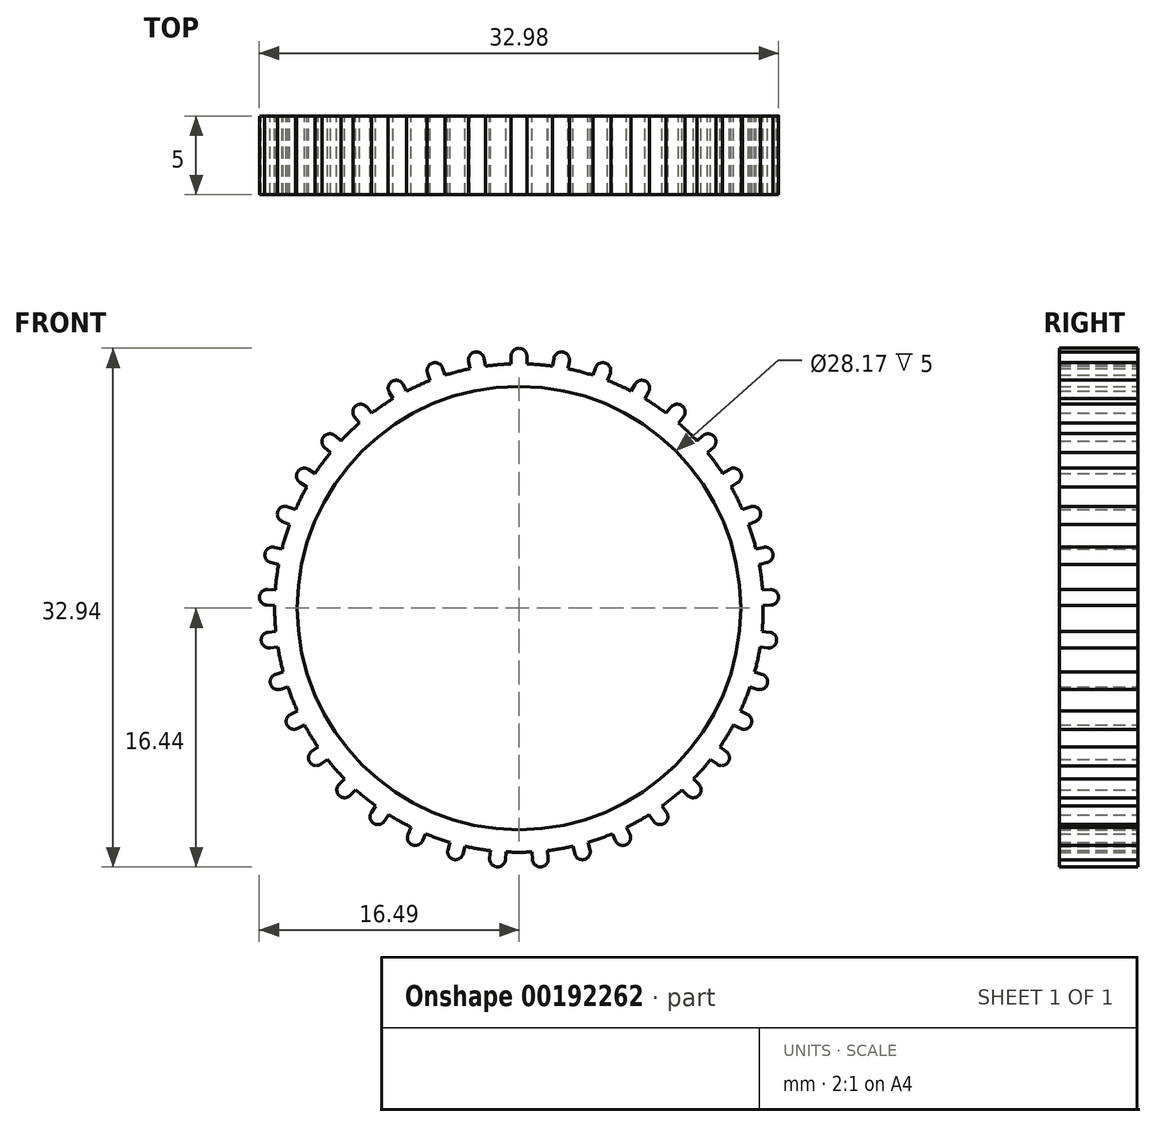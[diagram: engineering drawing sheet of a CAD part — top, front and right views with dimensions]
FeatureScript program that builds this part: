
annotation { "Feature Type Name" : "Feature", "Feature Type Description" : "" }
export const myFeature = defineFeature(function(context is Context, id is Id, definition is map)
    precondition{}
    {
        {
            var Q0;
            Q0=qCreatedBy(makeId("Front.planeOp"),FACE);
            var sketch = newSketch(context, id + "F0", { "sketchPlane" : qUnion([Q0])});
            skCircle(sketch, "E0", {"center": v(0, 0) * mm, "radius": 16.5 * mm});
            skLineSegment(sketch, "E1.bottom", {"start": v(0, 16.5) * mm, "end": v(0, 16.5) * mm});
            skLineSegment(sketch, "E1.top", {"start": v(0.5, 14.5) * mm, "end": v(-0.5, 14.5) * mm});
            skLineSegment(sketch, "E1.left", {"start": v(0.5, 16) * mm, "end": v(0.5, 14.5) * mm});
            skLineSegment(sketch, "E1.right", {"start": v(-0.5, 16) * mm, "end": v(-0.5, 14.5) * mm});
            skPoint(sketch, "E1.middle", {"position": v(0, 15.5) * mm});
            skPoint(sketch, "E2.visualSharp", {"position": v(-0.5, 16.5) * mm});
            skArc(sketch, "E2.filletArc", {"start": v(0, 16.5) * mm, "mid": v(-0.35, 16.35) * mm, "end": v(-0.5, 16) * mm});
            skPoint(sketch, "E3.visualSharp", {"position": v(0.5, 16.5) * mm});
            skArc(sketch, "E3.filletArc", {"start": v(0.5, 16) * mm, "mid": v(0.35, 16.35) * mm, "end": v(0, 16.5) * mm});
            skPoint(sketch, "E4.1.0", {"position": v(-3.28, 16.18) * mm});
            skArc(sketch, "E4.1.1", {"start": v(-2.21, 15.85) * mm, "mid": v(-2.42, 16.18) * mm, "end": v(-2.79, 16.26) * mm});
            skArc(sketch, "E4.1.2", {"start": v(-2.79, 16.26) * mm, "mid": v(-3.11, 16.06) * mm, "end": v(-3.2, 15.69) * mm});
            skLineSegment(sketch, "E4.1.3", {"start": v(-3.2, 15.69) * mm, "end": v(-2.94, 14.2) * mm});
            skLineSegment(sketch, "E4.1.4", {"start": v(-1.96, 14.38) * mm, "end": v(-2.94, 14.2) * mm});
            skPoint(sketch, "E4.1.5", {"position": v(-2.62, 15.28) * mm});
            skPoint(sketch, "E4.1.6", {"position": v(-2.3, 16.35) * mm});
            skLineSegment(sketch, "E4.1.7", {"start": v(-2.21, 15.85) * mm, "end": v(-1.96, 14.38) * mm});
            skPoint(sketch, "E4.2.0", {"position": v(-5.97, 15.4) * mm});
            skArc(sketch, "E4.2.1", {"start": v(-4.86, 15.25) * mm, "mid": v(-5.11, 15.54) * mm, "end": v(-5.5, 15.56) * mm});
            skArc(sketch, "E4.2.2", {"start": v(-5.5, 15.56) * mm, "mid": v(-5.78, 15.3) * mm, "end": v(-5.8, 14.92) * mm});
            skLineSegment(sketch, "E4.2.3", {"start": v(-5.8, 14.92) * mm, "end": v(-5.3, 13.5) * mm});
            skLineSegment(sketch, "E4.2.4", {"start": v(-4.36, 13.84) * mm, "end": v(-5.3, 13.5) * mm});
            skPoint(sketch, "E4.2.5", {"position": v(-5.16, 14.61) * mm});
            skPoint(sketch, "E4.2.6", {"position": v(-5.03, 15.72) * mm});
            skLineSegment(sketch, "E4.2.7", {"start": v(-4.86, 15.25) * mm, "end": v(-4.36, 13.84) * mm});
            skPoint(sketch, "E4.3.0", {"position": v(-8.48, 14.16) * mm});
            skArc(sketch, "E4.3.1", {"start": v(-7.37, 14.21) * mm, "mid": v(-7.67, 14.45) * mm, "end": v(-8.05, 14.4) * mm});
            skArc(sketch, "E4.3.2", {"start": v(-8.05, 14.4) * mm, "mid": v(-8.28, 14.1) * mm, "end": v(-8.24, 13.72) * mm});
            skLineSegment(sketch, "E4.3.3", {"start": v(-8.24, 13.72) * mm, "end": v(-7.5, 12.41) * mm});
            skLineSegment(sketch, "E4.3.4", {"start": v(-6.64, 12.9) * mm, "end": v(-7.5, 12.41) * mm});
            skPoint(sketch, "E4.3.5", {"position": v(-7.56, 13.53) * mm});
            skPoint(sketch, "E4.3.6", {"position": v(-7.61, 14.65) * mm});
            skLineSegment(sketch, "E4.3.7", {"start": v(-7.37, 14.21) * mm, "end": v(-6.64, 12.9) * mm});
            skPoint(sketch, "E4.4.0", {"position": v(-10.75, 12.52) * mm});
            skArc(sketch, "E4.4.1", {"start": v(-9.66, 12.76) * mm, "mid": v(-10, 12.95) * mm, "end": v(-10.37, 12.84) * mm});
            skArc(sketch, "E4.4.2", {"start": v(-10.37, 12.84) * mm, "mid": v(-10.55, 12.5) * mm, "end": v(-10.44, 12.13) * mm});
            skLineSegment(sketch, "E4.4.3", {"start": v(-10.44, 12.13) * mm, "end": v(-9.5, 10.97) * mm});
            skLineSegment(sketch, "E4.4.4", {"start": v(-8.72, 11.6) * mm, "end": v(-9.5, 10.97) * mm});
            skPoint(sketch, "E4.4.5", {"position": v(-9.74, 12.06) * mm});
            skPoint(sketch, "E4.4.6", {"position": v(-9.98, 13.15) * mm});
            skLineSegment(sketch, "E4.4.7", {"start": v(-9.66, 12.76) * mm, "end": v(-8.72, 11.6) * mm});
            skPoint(sketch, "E4.5.0", {"position": v(-12.72, 10.53) * mm});
            skArc(sketch, "E4.5.1", {"start": v(-11.68, 10.95) * mm, "mid": v(-12.04, 11.07) * mm, "end": v(-12.39, 10.9) * mm});
            skArc(sketch, "E4.5.2", {"start": v(-12.39, 10.9) * mm, "mid": v(-12.5, 10.54) * mm, "end": v(-12.34, 10.2) * mm});
            skLineSegment(sketch, "E4.5.3", {"start": v(-12.34, 10.2) * mm, "end": v(-11.22, 9.2) * mm});
            skLineSegment(sketch, "E4.5.4", {"start": v(-10.55, 9.96) * mm, "end": v(-11.22, 9.2) * mm});
            skPoint(sketch, "E4.5.5", {"position": v(-11.64, 10.24) * mm});
            skPoint(sketch, "E4.5.6", {"position": v(-12.06, 11.28) * mm});
            skLineSegment(sketch, "E4.5.7", {"start": v(-11.68, 10.95) * mm, "end": v(-10.55, 9.96) * mm});
            skPoint(sketch, "E4.6.0", {"position": v(-14.31, 8.23) * mm});
            skArc(sketch, "E4.6.1", {"start": v(-13.36, 8.81) * mm, "mid": v(-13.74, 8.88) * mm, "end": v(-14.05, 8.65) * mm});
            skArc(sketch, "E4.6.2", {"start": v(-14.05, 8.65) * mm, "mid": v(-14.11, 8.27) * mm, "end": v(-13.89, 7.96) * mm});
            skLineSegment(sketch, "E4.6.3", {"start": v(-13.89, 7.96) * mm, "end": v(-12.6, 7.18) * mm});
            skLineSegment(sketch, "E4.6.4", {"start": v(-12.09, 8.03) * mm, "end": v(-12.6, 7.18) * mm});
            skPoint(sketch, "E4.6.5", {"position": v(-13.2, 8.13) * mm});
            skPoint(sketch, "E4.6.6", {"position": v(-13.79, 9.08) * mm});
            skLineSegment(sketch, "E4.6.7", {"start": v(-13.36, 8.81) * mm, "end": v(-12.09, 8.03) * mm});
            skPoint(sketch, "E4.7.0", {"position": v(-15.5, 5.69) * mm});
            skArc(sketch, "E4.7.1", {"start": v(-14.66, 6.43) * mm, "mid": v(-15.04, 6.43) * mm, "end": v(-15.31, 6.15) * mm});
            skArc(sketch, "E4.7.2", {"start": v(-15.31, 6.15) * mm, "mid": v(-15.3, 5.77) * mm, "end": v(-15.03, 5.5) * mm});
            skLineSegment(sketch, "E4.7.3", {"start": v(-15.03, 5.5) * mm, "end": v(-13.64, 4.94) * mm});
            skLineSegment(sketch, "E4.7.4", {"start": v(-13.27, 5.87) * mm, "end": v(-13.64, 4.94) * mm});
            skPoint(sketch, "E4.7.5", {"position": v(-14.38, 5.78) * mm});
            skPoint(sketch, "E4.7.6", {"position": v(-15.12, 6.62) * mm});
            skLineSegment(sketch, "E4.7.7", {"start": v(-14.66, 6.43) * mm, "end": v(-13.27, 5.87) * mm});
            skPoint(sketch, "E4.8.0", {"position": v(-16.24, 2.99) * mm});
            skArc(sketch, "E4.8.1", {"start": v(-15.54, 3.86) * mm, "mid": v(-15.91, 3.8) * mm, "end": v(-16.13, 3.48) * mm});
            skArc(sketch, "E4.8.2", {"start": v(-16.13, 3.48) * mm, "mid": v(-16.06, 3.1) * mm, "end": v(-15.75, 2.88) * mm});
            skLineSegment(sketch, "E4.8.3", {"start": v(-15.75, 2.88) * mm, "end": v(-14.28, 2.57) * mm});
            skLineSegment(sketch, "E4.8.4", {"start": v(-14.07, 3.54) * mm, "end": v(-14.28, 2.57) * mm});
            skPoint(sketch, "E4.8.5", {"position": v(-15.15, 3.27) * mm});
            skPoint(sketch, "E4.8.6", {"position": v(-16.02, 3.96) * mm});
            skLineSegment(sketch, "E4.8.7", {"start": v(-15.54, 3.86) * mm, "end": v(-14.07, 3.54) * mm});
            skPoint(sketch, "E4.9.0", {"position": v(-16.5, 0.2) * mm});
            skArc(sketch, "E4.9.1", {"start": v(-15.96, 1.18) * mm, "mid": v(-16.32, 1.05) * mm, "end": v(-16.49, 0.7) * mm});
            skArc(sketch, "E4.9.2", {"start": v(-16.49, 0.7) * mm, "mid": v(-16.35, 0.34) * mm, "end": v(-16, 0.18) * mm});
            skLineSegment(sketch, "E4.9.3", {"start": v(-16, 0.18) * mm, "end": v(-14.5, 0.12) * mm});
            skLineSegment(sketch, "E4.9.4", {"start": v(-14.47, 1.11) * mm, "end": v(-14.5, 0.12) * mm});
            skPoint(sketch, "E4.9.5", {"position": v(-15.49, 0.66) * mm});
            skPoint(sketch, "E4.9.6", {"position": v(-16.46, 1.2) * mm});
            skLineSegment(sketch, "E4.9.7", {"start": v(-15.96, 1.18) * mm, "end": v(-14.47, 1.11) * mm});
            skPoint(sketch, "E4.10.0", {"position": v(-16.3, -2.6) * mm});
            skArc(sketch, "E4.10.1", {"start": v(-15.93, -1.54) * mm, "mid": v(-16.27, -1.73) * mm, "end": v(-16.37, -2.1) * mm});
            skArc(sketch, "E4.10.2", {"start": v(-16.37, -2.1) * mm, "mid": v(-16.18, -2.43) * mm, "end": v(-15.8, -2.53) * mm});
            skLineSegment(sketch, "E4.10.3", {"start": v(-15.8, -2.53) * mm, "end": v(-14.32, -2.34) * mm});
            skLineSegment(sketch, "E4.10.4", {"start": v(-14.45, -1.35) * mm, "end": v(-14.32, -2.34) * mm});
            skPoint(sketch, "E4.10.5", {"position": v(-15.37, -1.97) * mm});
            skPoint(sketch, "E4.10.6", {"position": v(-16.43, -1.6) * mm});
            skLineSegment(sketch, "E4.10.7", {"start": v(-15.93, -1.54) * mm, "end": v(-14.45, -1.35) * mm});
            skPoint(sketch, "E4.11.0", {"position": v(-15.63, -5.3) * mm});
            skArc(sketch, "E4.11.1", {"start": v(-15.45, -4.2) * mm, "mid": v(-15.74, -4.45) * mm, "end": v(-15.78, -4.83) * mm});
            skArc(sketch, "E4.11.2", {"start": v(-15.78, -4.83) * mm, "mid": v(-15.53, -5.13) * mm, "end": v(-15.15, -5.16) * mm});
            skLineSegment(sketch, "E4.11.3", {"start": v(-15.15, -5.16) * mm, "end": v(-13.72, -4.72) * mm});
            skLineSegment(sketch, "E4.11.4", {"start": v(-14.01, -3.77) * mm, "end": v(-13.72, -4.72) * mm});
            skPoint(sketch, "E4.11.5", {"position": v(-14.82, -4.54) * mm});
            skPoint(sketch, "E4.11.6", {"position": v(-15.92, -4.35) * mm});
            skLineSegment(sketch, "E4.11.7", {"start": v(-15.45, -4.2) * mm, "end": v(-14.01, -3.77) * mm});
            skPoint(sketch, "E4.12.0", {"position": v(-14.5, -7.87) * mm});
            skArc(sketch, "E4.12.1", {"start": v(-14.51, -6.76) * mm, "mid": v(-14.76, -7.05) * mm, "end": v(-14.73, -7.43) * mm});
            skArc(sketch, "E4.12.2", {"start": v(-14.73, -7.43) * mm, "mid": v(-14.44, -7.68) * mm, "end": v(-14.06, -7.65) * mm});
            skLineSegment(sketch, "E4.12.3", {"start": v(-14.06, -7.65) * mm, "end": v(-12.72, -6.97) * mm});
            skLineSegment(sketch, "E4.12.4", {"start": v(-13.17, -6.08) * mm, "end": v(-12.72, -6.97) * mm});
            skPoint(sketch, "E4.12.5", {"position": v(-13.84, -6.98) * mm});
            skPoint(sketch, "E4.12.6", {"position": v(-14.96, -6.98) * mm});
            skLineSegment(sketch, "E4.12.7", {"start": v(-14.51, -6.76) * mm, "end": v(-13.17, -6.08) * mm});
            skPoint(sketch, "E4.13.0", {"position": v(-12.97, -10.21) * mm});
            skArc(sketch, "E4.13.1", {"start": v(-13.16, -9.11) * mm, "mid": v(-13.36, -9.44) * mm, "end": v(-13.27, -9.81) * mm});
            skArc(sketch, "E4.13.2", {"start": v(-13.27, -9.81) * mm, "mid": v(-12.94, -10) * mm, "end": v(-12.57, -9.92) * mm});
            skLineSegment(sketch, "E4.13.3", {"start": v(-12.57, -9.92) * mm, "end": v(-11.36, -9.02) * mm});
            skLineSegment(sketch, "E4.13.4", {"start": v(-11.96, -8.22) * mm, "end": v(-11.36, -9.02) * mm});
            skPoint(sketch, "E4.13.5", {"position": v(-12.46, -9.22) * mm});
            skPoint(sketch, "E4.13.6", {"position": v(-13.56, -9.4) * mm});
            skLineSegment(sketch, "E4.13.7", {"start": v(-13.16, -9.11) * mm, "end": v(-11.96, -8.22) * mm});
            skPoint(sketch, "E4.14.0", {"position": v(-11.06, -12.26) * mm});
            skArc(sketch, "E4.14.1", {"start": v(-11.43, -11.2) * mm, "mid": v(-11.57, -11.56) * mm, "end": v(-11.42, -11.91) * mm});
            skArc(sketch, "E4.14.2", {"start": v(-11.42, -11.91) * mm, "mid": v(-11.06, -12.05) * mm, "end": v(-10.71, -11.9) * mm});
            skLineSegment(sketch, "E4.14.3", {"start": v(-10.71, -11.9) * mm, "end": v(-9.67, -10.81) * mm});
            skLineSegment(sketch, "E4.14.4", {"start": v(-10.4, -10.12) * mm, "end": v(-9.67, -10.81) * mm});
            skPoint(sketch, "E4.14.5", {"position": v(-10.73, -11.2) * mm});
            skPoint(sketch, "E4.14.6", {"position": v(-11.78, -11.57) * mm});
            skLineSegment(sketch, "E4.14.7", {"start": v(-11.43, -11.2) * mm, "end": v(-10.4, -10.12) * mm});
            skPoint(sketch, "E4.15.0", {"position": v(-8.83, -13.95) * mm});
            skArc(sketch, "E4.15.1", {"start": v(-9.37, -12.98) * mm, "mid": v(-9.45, -13.35) * mm, "end": v(-9.24, -13.67) * mm});
            skArc(sketch, "E4.15.2", {"start": v(-9.24, -13.67) * mm, "mid": v(-8.86, -13.75) * mm, "end": v(-8.55, -13.54) * mm});
            skLineSegment(sketch, "E4.15.3", {"start": v(-8.55, -13.54) * mm, "end": v(-7.7, -12.3) * mm});
            skLineSegment(sketch, "E4.15.4", {"start": v(-8.53, -11.73) * mm, "end": v(-7.7, -12.3) * mm});
            skPoint(sketch, "E4.15.5", {"position": v(-8.68, -12.84) * mm});
            skPoint(sketch, "E4.15.6", {"position": v(-9.65, -13.4) * mm});
            skLineSegment(sketch, "E4.15.7", {"start": v(-9.37, -12.98) * mm, "end": v(-8.53, -11.73) * mm});
            skPoint(sketch, "E4.16.0", {"position": v(-6.34, -15.24) * mm});
            skArc(sketch, "E4.16.1", {"start": v(-7.05, -14.37) * mm, "mid": v(-7.06, -14.76) * mm, "end": v(-6.8, -15.04) * mm});
            skArc(sketch, "E4.16.2", {"start": v(-6.8, -15.04) * mm, "mid": v(-6.41, -15.05) * mm, "end": v(-6.13, -14.79) * mm});
            skLineSegment(sketch, "E4.16.3", {"start": v(-6.13, -14.79) * mm, "end": v(-5.52, -13.42) * mm});
            skLineSegment(sketch, "E4.16.4", {"start": v(-6.43, -13) * mm, "end": v(-5.52, -13.42) * mm});
            skPoint(sketch, "E4.16.5", {"position": v(-6.38, -14.12) * mm});
            skPoint(sketch, "E4.16.6", {"position": v(-7.25, -14.83) * mm});
            skLineSegment(sketch, "E4.16.7", {"start": v(-7.05, -14.37) * mm, "end": v(-6.43, -13) * mm});
            skPoint(sketch, "E4.17.0", {"position": v(-3.67, -16.1) * mm});
            skArc(sketch, "E4.17.1", {"start": v(-4.52, -15.36) * mm, "mid": v(-4.46, -15.74) * mm, "end": v(-4.16, -15.97) * mm});
            skArc(sketch, "E4.17.2", {"start": v(-4.16, -15.97) * mm, "mid": v(-3.78, -15.91) * mm, "end": v(-3.55, -15.6) * mm});
            skLineSegment(sketch, "E4.17.3", {"start": v(-3.55, -15.6) * mm, "end": v(-3.17, -14.16) * mm});
            skLineSegment(sketch, "E4.17.4", {"start": v(-4.14, -13.9) * mm, "end": v(-3.17, -14.16) * mm});
            skPoint(sketch, "E4.17.5", {"position": v(-3.9, -15) * mm});
            skPoint(sketch, "E4.17.6", {"position": v(-4.64, -15.84) * mm});
            skLineSegment(sketch, "E4.17.7", {"start": v(-4.52, -15.36) * mm, "end": v(-4.14, -13.9) * mm});
            skPoint(sketch, "E4.18.0", {"position": v(-0.9, -16.48) * mm});
            skArc(sketch, "E4.18.1", {"start": v(-1.86, -15.9) * mm, "mid": v(-1.74, -16.26) * mm, "end": v(-1.4, -16.44) * mm});
            skArc(sketch, "E4.18.2", {"start": v(-1.4, -16.44) * mm, "mid": v(-1.03, -16.32) * mm, "end": v(-0.86, -15.98) * mm});
            skLineSegment(sketch, "E4.18.3", {"start": v(-0.86, -15.98) * mm, "end": v(-0.73, -14.5) * mm});
            skLineSegment(sketch, "E4.18.4", {"start": v(-1.73, -14.4) * mm, "end": v(-0.73, -14.5) * mm});
            skPoint(sketch, "E4.18.5", {"position": v(-1.31, -15.44) * mm});
            skPoint(sketch, "E4.18.6", {"position": v(-1.9, -16.4) * mm});
            skLineSegment(sketch, "E4.18.7", {"start": v(-1.86, -15.9) * mm, "end": v(-1.73, -14.4) * mm});
            skPoint(sketch, "E4.19.0", {"position": v(1.9, -16.4) * mm});
            skArc(sketch, "E4.19.1", {"start": v(0.86, -15.98) * mm, "mid": v(1.03, -16.32) * mm, "end": v(1.4, -16.44) * mm});
            skArc(sketch, "E4.19.2", {"start": v(1.4, -16.44) * mm, "mid": v(1.74, -16.26) * mm, "end": v(1.86, -15.9) * mm});
            skLineSegment(sketch, "E4.19.3", {"start": v(1.86, -15.9) * mm, "end": v(1.73, -14.4) * mm});
            skLineSegment(sketch, "E4.19.4", {"start": v(0.73, -14.5) * mm, "end": v(1.73, -14.4) * mm});
            skPoint(sketch, "E4.19.5", {"position": v(1.31, -15.44) * mm});
            skPoint(sketch, "E4.19.6", {"position": v(0.9, -16.48) * mm});
            skLineSegment(sketch, "E4.19.7", {"start": v(0.86, -15.98) * mm, "end": v(0.73, -14.5) * mm});
            skPoint(sketch, "E4.20.0", {"position": v(4.64, -15.84) * mm});
            skArc(sketch, "E4.20.1", {"start": v(3.55, -15.6) * mm, "mid": v(3.78, -15.91) * mm, "end": v(4.16, -15.97) * mm});
            skArc(sketch, "E4.20.2", {"start": v(4.16, -15.97) * mm, "mid": v(4.46, -15.74) * mm, "end": v(4.52, -15.36) * mm});
            skLineSegment(sketch, "E4.20.3", {"start": v(4.52, -15.36) * mm, "end": v(4.14, -13.9) * mm});
            skLineSegment(sketch, "E4.20.4", {"start": v(3.17, -14.16) * mm, "end": v(4.14, -13.9) * mm});
            skPoint(sketch, "E4.20.5", {"position": v(3.9, -15) * mm});
            skPoint(sketch, "E4.20.6", {"position": v(3.67, -16.1) * mm});
            skLineSegment(sketch, "E4.20.7", {"start": v(3.55, -15.6) * mm, "end": v(3.17, -14.16) * mm});
            skPoint(sketch, "E4.21.0", {"position": v(7.25, -14.83) * mm});
            skArc(sketch, "E4.21.1", {"start": v(6.13, -14.79) * mm, "mid": v(6.41, -15.05) * mm, "end": v(6.8, -15.04) * mm});
            skArc(sketch, "E4.21.2", {"start": v(6.8, -15.04) * mm, "mid": v(7.06, -14.76) * mm, "end": v(7.05, -14.37) * mm});
            skLineSegment(sketch, "E4.21.3", {"start": v(7.05, -14.37) * mm, "end": v(6.43, -13) * mm});
            skLineSegment(sketch, "E4.21.4", {"start": v(5.52, -13.42) * mm, "end": v(6.43, -13) * mm});
            skPoint(sketch, "E4.21.5", {"position": v(6.38, -14.12) * mm});
            skPoint(sketch, "E4.21.6", {"position": v(6.34, -15.24) * mm});
            skLineSegment(sketch, "E4.21.7", {"start": v(6.13, -14.79) * mm, "end": v(5.52, -13.42) * mm});
            skPoint(sketch, "E4.22.0", {"position": v(9.65, -13.4) * mm});
            skArc(sketch, "E4.22.1", {"start": v(8.55, -13.54) * mm, "mid": v(8.86, -13.75) * mm, "end": v(9.24, -13.67) * mm});
            skArc(sketch, "E4.22.2", {"start": v(9.24, -13.67) * mm, "mid": v(9.45, -13.35) * mm, "end": v(9.37, -12.98) * mm});
            skLineSegment(sketch, "E4.22.3", {"start": v(9.37, -12.98) * mm, "end": v(8.53, -11.73) * mm});
            skLineSegment(sketch, "E4.22.4", {"start": v(7.7, -12.3) * mm, "end": v(8.53, -11.73) * mm});
            skPoint(sketch, "E4.22.5", {"position": v(8.68, -12.84) * mm});
            skPoint(sketch, "E4.22.6", {"position": v(8.83, -13.95) * mm});
            skLineSegment(sketch, "E4.22.7", {"start": v(8.55, -13.54) * mm, "end": v(7.7, -12.3) * mm});
            skPoint(sketch, "E4.23.0", {"position": v(11.78, -11.57) * mm});
            skArc(sketch, "E4.23.1", {"start": v(10.71, -11.9) * mm, "mid": v(11.06, -12.05) * mm, "end": v(11.42, -11.91) * mm});
            skArc(sketch, "E4.23.2", {"start": v(11.42, -11.91) * mm, "mid": v(11.57, -11.56) * mm, "end": v(11.43, -11.2) * mm});
            skLineSegment(sketch, "E4.23.3", {"start": v(11.43, -11.2) * mm, "end": v(10.4, -10.12) * mm});
            skLineSegment(sketch, "E4.23.4", {"start": v(9.67, -10.81) * mm, "end": v(10.4, -10.12) * mm});
            skPoint(sketch, "E4.23.5", {"position": v(10.73, -11.2) * mm});
            skPoint(sketch, "E4.23.6", {"position": v(11.06, -12.26) * mm});
            skLineSegment(sketch, "E4.23.7", {"start": v(10.71, -11.9) * mm, "end": v(9.67, -10.81) * mm});
            skPoint(sketch, "E4.24.0", {"position": v(13.56, -9.4) * mm});
            skArc(sketch, "E4.24.1", {"start": v(12.57, -9.92) * mm, "mid": v(12.94, -10) * mm, "end": v(13.27, -9.81) * mm});
            skArc(sketch, "E4.24.2", {"start": v(13.27, -9.81) * mm, "mid": v(13.36, -9.44) * mm, "end": v(13.16, -9.11) * mm});
            skLineSegment(sketch, "E4.24.3", {"start": v(13.16, -9.11) * mm, "end": v(11.96, -8.22) * mm});
            skLineSegment(sketch, "E4.24.4", {"start": v(11.36, -9.02) * mm, "end": v(11.96, -8.22) * mm});
            skPoint(sketch, "E4.24.5", {"position": v(12.46, -9.22) * mm});
            skPoint(sketch, "E4.24.6", {"position": v(12.97, -10.21) * mm});
            skLineSegment(sketch, "E4.24.7", {"start": v(12.57, -9.92) * mm, "end": v(11.36, -9.02) * mm});
            skPoint(sketch, "E4.25.0", {"position": v(14.96, -6.98) * mm});
            skArc(sketch, "E4.25.1", {"start": v(14.06, -7.65) * mm, "mid": v(14.44, -7.68) * mm, "end": v(14.73, -7.43) * mm});
            skArc(sketch, "E4.25.2", {"start": v(14.73, -7.43) * mm, "mid": v(14.76, -7.05) * mm, "end": v(14.51, -6.76) * mm});
            skLineSegment(sketch, "E4.25.3", {"start": v(14.51, -6.76) * mm, "end": v(13.17, -6.08) * mm});
            skLineSegment(sketch, "E4.25.4", {"start": v(12.72, -6.97) * mm, "end": v(13.17, -6.08) * mm});
            skPoint(sketch, "E4.25.5", {"position": v(13.84, -6.98) * mm});
            skPoint(sketch, "E4.25.6", {"position": v(14.5, -7.87) * mm});
            skLineSegment(sketch, "E4.25.7", {"start": v(14.06, -7.65) * mm, "end": v(12.72, -6.97) * mm});
            skPoint(sketch, "E4.26.0", {"position": v(15.92, -4.35) * mm});
            skArc(sketch, "E4.26.1", {"start": v(15.15, -5.16) * mm, "mid": v(15.53, -5.13) * mm, "end": v(15.78, -4.83) * mm});
            skArc(sketch, "E4.26.2", {"start": v(15.78, -4.83) * mm, "mid": v(15.74, -4.45) * mm, "end": v(15.45, -4.2) * mm});
            skLineSegment(sketch, "E4.26.3", {"start": v(15.45, -4.2) * mm, "end": v(14.01, -3.77) * mm});
            skLineSegment(sketch, "E4.26.4", {"start": v(13.72, -4.72) * mm, "end": v(14.01, -3.77) * mm});
            skPoint(sketch, "E4.26.5", {"position": v(14.82, -4.54) * mm});
            skPoint(sketch, "E4.26.6", {"position": v(15.63, -5.3) * mm});
            skLineSegment(sketch, "E4.26.7", {"start": v(15.15, -5.16) * mm, "end": v(13.72, -4.72) * mm});
            skPoint(sketch, "E4.27.0", {"position": v(16.43, -1.6) * mm});
            skArc(sketch, "E4.27.1", {"start": v(15.8, -2.53) * mm, "mid": v(16.18, -2.43) * mm, "end": v(16.37, -2.1) * mm});
            skArc(sketch, "E4.27.2", {"start": v(16.37, -2.1) * mm, "mid": v(16.27, -1.73) * mm, "end": v(15.93, -1.54) * mm});
            skLineSegment(sketch, "E4.27.3", {"start": v(15.93, -1.54) * mm, "end": v(14.45, -1.35) * mm});
            skLineSegment(sketch, "E4.27.4", {"start": v(14.32, -2.34) * mm, "end": v(14.45, -1.35) * mm});
            skPoint(sketch, "E4.27.5", {"position": v(15.37, -1.97) * mm});
            skPoint(sketch, "E4.27.6", {"position": v(16.3, -2.6) * mm});
            skLineSegment(sketch, "E4.27.7", {"start": v(15.8, -2.53) * mm, "end": v(14.32, -2.34) * mm});
            skPoint(sketch, "E4.28.0", {"position": v(16.46, 1.2) * mm});
            skArc(sketch, "E4.28.1", {"start": v(16, 0.18) * mm, "mid": v(16.35, 0.34) * mm, "end": v(16.49, 0.7) * mm});
            skArc(sketch, "E4.28.2", {"start": v(16.49, 0.7) * mm, "mid": v(16.32, 1.05) * mm, "end": v(15.96, 1.18) * mm});
            skLineSegment(sketch, "E4.28.3", {"start": v(15.96, 1.18) * mm, "end": v(14.47, 1.11) * mm});
            skLineSegment(sketch, "E4.28.4", {"start": v(14.5, 0.12) * mm, "end": v(14.47, 1.11) * mm});
            skPoint(sketch, "E4.28.5", {"position": v(15.49, 0.66) * mm});
            skPoint(sketch, "E4.28.6", {"position": v(16.5, 0.2) * mm});
            skLineSegment(sketch, "E4.28.7", {"start": v(16, 0.18) * mm, "end": v(14.5, 0.12) * mm});
            skPoint(sketch, "E4.29.0", {"position": v(16.02, 3.96) * mm});
            skArc(sketch, "E4.29.1", {"start": v(15.75, 2.88) * mm, "mid": v(16.06, 3.1) * mm, "end": v(16.13, 3.48) * mm});
            skArc(sketch, "E4.29.2", {"start": v(16.13, 3.48) * mm, "mid": v(15.91, 3.8) * mm, "end": v(15.54, 3.86) * mm});
            skLineSegment(sketch, "E4.29.3", {"start": v(15.54, 3.86) * mm, "end": v(14.07, 3.54) * mm});
            skLineSegment(sketch, "E4.29.4", {"start": v(14.28, 2.57) * mm, "end": v(14.07, 3.54) * mm});
            skPoint(sketch, "E4.29.5", {"position": v(15.15, 3.27) * mm});
            skPoint(sketch, "E4.29.6", {"position": v(16.24, 2.99) * mm});
            skLineSegment(sketch, "E4.29.7", {"start": v(15.75, 2.88) * mm, "end": v(14.28, 2.57) * mm});
            skPoint(sketch, "E4.30.0", {"position": v(15.12, 6.62) * mm});
            skArc(sketch, "E4.30.1", {"start": v(15.03, 5.5) * mm, "mid": v(15.3, 5.77) * mm, "end": v(15.31, 6.15) * mm});
            skArc(sketch, "E4.30.2", {"start": v(15.31, 6.15) * mm, "mid": v(15.04, 6.43) * mm, "end": v(14.66, 6.43) * mm});
            skLineSegment(sketch, "E4.30.3", {"start": v(14.66, 6.43) * mm, "end": v(13.27, 5.87) * mm});
            skLineSegment(sketch, "E4.30.4", {"start": v(13.64, 4.94) * mm, "end": v(13.27, 5.87) * mm});
            skPoint(sketch, "E4.30.5", {"position": v(14.38, 5.78) * mm});
            skPoint(sketch, "E4.30.6", {"position": v(15.5, 5.69) * mm});
            skLineSegment(sketch, "E4.30.7", {"start": v(15.03, 5.5) * mm, "end": v(13.64, 4.94) * mm});
            skPoint(sketch, "E4.31.0", {"position": v(13.79, 9.08) * mm});
            skArc(sketch, "E4.31.1", {"start": v(13.89, 7.96) * mm, "mid": v(14.11, 8.27) * mm, "end": v(14.05, 8.65) * mm});
            skArc(sketch, "E4.31.2", {"start": v(14.05, 8.65) * mm, "mid": v(13.74, 8.88) * mm, "end": v(13.36, 8.81) * mm});
            skLineSegment(sketch, "E4.31.3", {"start": v(13.36, 8.81) * mm, "end": v(12.09, 8.03) * mm});
            skLineSegment(sketch, "E4.31.4", {"start": v(12.6, 7.18) * mm, "end": v(12.09, 8.03) * mm});
            skPoint(sketch, "E4.31.5", {"position": v(13.2, 8.13) * mm});
            skPoint(sketch, "E4.31.6", {"position": v(14.31, 8.23) * mm});
            skLineSegment(sketch, "E4.31.7", {"start": v(13.89, 7.96) * mm, "end": v(12.6, 7.18) * mm});
            skPoint(sketch, "E4.32.0", {"position": v(12.06, 11.28) * mm});
            skArc(sketch, "E4.32.1", {"start": v(12.34, 10.2) * mm, "mid": v(12.5, 10.54) * mm, "end": v(12.39, 10.9) * mm});
            skArc(sketch, "E4.32.2", {"start": v(12.39, 10.9) * mm, "mid": v(12.04, 11.07) * mm, "end": v(11.68, 10.95) * mm});
            skLineSegment(sketch, "E4.32.3", {"start": v(11.68, 10.95) * mm, "end": v(10.55, 9.96) * mm});
            skLineSegment(sketch, "E4.32.4", {"start": v(11.22, 9.2) * mm, "end": v(10.55, 9.96) * mm});
            skPoint(sketch, "E4.32.5", {"position": v(11.64, 10.24) * mm});
            skPoint(sketch, "E4.32.6", {"position": v(12.72, 10.53) * mm});
            skLineSegment(sketch, "E4.32.7", {"start": v(12.34, 10.2) * mm, "end": v(11.22, 9.2) * mm});
            skPoint(sketch, "E4.33.0", {"position": v(9.98, 13.15) * mm});
            skArc(sketch, "E4.33.1", {"start": v(10.44, 12.13) * mm, "mid": v(10.55, 12.5) * mm, "end": v(10.37, 12.84) * mm});
            skArc(sketch, "E4.33.2", {"start": v(10.37, 12.84) * mm, "mid": v(10, 12.95) * mm, "end": v(9.66, 12.76) * mm});
            skLineSegment(sketch, "E4.33.3", {"start": v(9.66, 12.76) * mm, "end": v(8.72, 11.6) * mm});
            skLineSegment(sketch, "E4.33.4", {"start": v(9.5, 10.97) * mm, "end": v(8.72, 11.6) * mm});
            skPoint(sketch, "E4.33.5", {"position": v(9.74, 12.06) * mm});
            skPoint(sketch, "E4.33.6", {"position": v(10.75, 12.52) * mm});
            skLineSegment(sketch, "E4.33.7", {"start": v(10.44, 12.13) * mm, "end": v(9.5, 10.97) * mm});
            skPoint(sketch, "E4.34.0", {"position": v(7.61, 14.65) * mm});
            skArc(sketch, "E4.34.1", {"start": v(8.24, 13.72) * mm, "mid": v(8.28, 14.1) * mm, "end": v(8.05, 14.4) * mm});
            skArc(sketch, "E4.34.2", {"start": v(8.05, 14.4) * mm, "mid": v(7.67, 14.45) * mm, "end": v(7.37, 14.21) * mm});
            skLineSegment(sketch, "E4.34.3", {"start": v(7.37, 14.21) * mm, "end": v(6.64, 12.9) * mm});
            skLineSegment(sketch, "E4.34.4", {"start": v(7.5, 12.41) * mm, "end": v(6.64, 12.9) * mm});
            skPoint(sketch, "E4.34.5", {"position": v(7.56, 13.53) * mm});
            skPoint(sketch, "E4.34.6", {"position": v(8.48, 14.16) * mm});
            skLineSegment(sketch, "E4.34.7", {"start": v(8.24, 13.72) * mm, "end": v(7.5, 12.41) * mm});
            skPoint(sketch, "E4.35.0", {"position": v(5.03, 15.72) * mm});
            skArc(sketch, "E4.35.1", {"start": v(5.8, 14.92) * mm, "mid": v(5.78, 15.3) * mm, "end": v(5.5, 15.56) * mm});
            skArc(sketch, "E4.35.2", {"start": v(5.5, 15.56) * mm, "mid": v(5.11, 15.54) * mm, "end": v(4.86, 15.25) * mm});
            skLineSegment(sketch, "E4.35.3", {"start": v(4.86, 15.25) * mm, "end": v(4.36, 13.84) * mm});
            skLineSegment(sketch, "E4.35.4", {"start": v(5.3, 13.5) * mm, "end": v(4.36, 13.84) * mm});
            skPoint(sketch, "E4.35.5", {"position": v(5.16, 14.61) * mm});
            skPoint(sketch, "E4.35.6", {"position": v(5.97, 15.4) * mm});
            skLineSegment(sketch, "E4.35.7", {"start": v(5.8, 14.92) * mm, "end": v(5.3, 13.5) * mm});
            skPoint(sketch, "E4.36.0", {"position": v(2.3, 16.35) * mm});
            skArc(sketch, "E4.36.1", {"start": v(3.2, 15.69) * mm, "mid": v(3.11, 16.06) * mm, "end": v(2.79, 16.26) * mm});
            skArc(sketch, "E4.36.2", {"start": v(2.79, 16.26) * mm, "mid": v(2.42, 16.18) * mm, "end": v(2.21, 15.85) * mm});
            skLineSegment(sketch, "E4.36.3", {"start": v(2.21, 15.85) * mm, "end": v(1.96, 14.38) * mm});
            skLineSegment(sketch, "E4.36.4", {"start": v(2.94, 14.2) * mm, "end": v(1.96, 14.38) * mm});
            skPoint(sketch, "E4.36.5", {"position": v(2.62, 15.28) * mm});
            skPoint(sketch, "E4.36.6", {"position": v(3.28, 16.18) * mm});
            skLineSegment(sketch, "E4.36.7", {"start": v(3.2, 15.69) * mm, "end": v(2.94, 14.2) * mm});
            skCircle(sketch, "E5", {"center": v(0, 0) * mm, "radius": 15.51 * mm});
            skCircle(sketch, "E6", {"center": v(0, 0) * mm, "radius": 14.09 * mm});
            skSolve(sketch);
        }
        {
            var Q0;
            {var subQ0=sQuery(id+"F0.wireOp",EDGE,"E4.8.4");Q0=makeQuery(id+"F0.imprint","IMPRINT",FACE,{"disambiguationData":[TD([[makeQuery(id+"F0.imprint","IMPRINT",EDGE,{"derivedFrom":subQ0}),-1.0]])]});}
            var Q1;
            {var subQ80=sQuery(id+"F0.wireOp",EDGE,"E1.top");Q1=makeQuery(id+"F0.imprint","IMPRINT",FACE,{"disambiguationData":[TD([[makeQuery(id+"F0.imprint","IMPRINT",EDGE,{"derivedFrom":subQ80}),1.0]])]});}
            var Q2;
            {var subQ0=sQuery(id+"F0.wireOp",EDGE,"E4.7.4");Q2=makeQuery(id+"F0.imprint","IMPRINT",FACE,{"disambiguationData":[TD([[makeQuery(id+"F0.imprint","IMPRINT",EDGE,{"derivedFrom":subQ0}),-1.0]])]});}
            var Q3;
            {var subQ1=sQuery(id+"F0.wireOp",EDGE,"E4.7.1");Q3=makeQuery(id+"F0.imprint","IMPRINT",FACE,{"disambiguationData":[TD([[makeQuery(id+"F0.imprint","IMPRINT",EDGE,{"derivedFrom":subQ1}),1.0]])]});}
            var Q4;
            {var subQ1=sQuery(id+"F0.wireOp",EDGE,"E4.8.1");Q4=makeQuery(id+"F0.imprint","IMPRINT",FACE,{"disambiguationData":[TD([[makeQuery(id+"F0.imprint","IMPRINT",EDGE,{"derivedFrom":subQ1}),1.0]])]});}
            var Q5;
            {var subQ1=sQuery(id+"F0.wireOp",EDGE,"E4.6.1");Q5=makeQuery(id+"F0.imprint","IMPRINT",FACE,{"disambiguationData":[TD([[makeQuery(id+"F0.imprint","IMPRINT",EDGE,{"derivedFrom":subQ1}),1.0]])]});}
            var Q6;
            {var subQ0=sQuery(id+"F0.wireOp",EDGE,"E4.6.4");Q6=makeQuery(id+"F0.imprint","IMPRINT",FACE,{"disambiguationData":[TD([[makeQuery(id+"F0.imprint","IMPRINT",EDGE,{"derivedFrom":subQ0}),-1.0]])]});}
            var Q7;
            {var subQ0=sQuery(id+"F0.wireOp",EDGE,"E4.5.4");Q7=makeQuery(id+"F0.imprint","IMPRINT",FACE,{"disambiguationData":[TD([[makeQuery(id+"F0.imprint","IMPRINT",EDGE,{"derivedFrom":subQ0}),-1.0]])]});}
            var Q8;
            {var subQ1=sQuery(id+"F0.wireOp",EDGE,"E4.5.1");Q8=makeQuery(id+"F0.imprint","IMPRINT",FACE,{"disambiguationData":[TD([[makeQuery(id+"F0.imprint","IMPRINT",EDGE,{"derivedFrom":subQ1}),1.0]])]});}
            var Q9;
            {var subQ1=sQuery(id+"F0.wireOp",EDGE,"E4.4.1");Q9=makeQuery(id+"F0.imprint","IMPRINT",FACE,{"disambiguationData":[TD([[makeQuery(id+"F0.imprint","IMPRINT",EDGE,{"derivedFrom":subQ1}),1.0]])]});}
            var Q10;
            {var subQ0=sQuery(id+"F0.wireOp",EDGE,"E4.4.4");Q10=makeQuery(id+"F0.imprint","IMPRINT",FACE,{"disambiguationData":[TD([[makeQuery(id+"F0.imprint","IMPRINT",EDGE,{"derivedFrom":subQ0}),-1.0]])]});}
            var Q11;
            {var subQ0=sQuery(id+"F0.wireOp",EDGE,"E4.3.4");Q11=makeQuery(id+"F0.imprint","IMPRINT",FACE,{"disambiguationData":[TD([[makeQuery(id+"F0.imprint","IMPRINT",EDGE,{"derivedFrom":subQ0}),-1.0]])]});}
            var Q12;
            {var subQ1=sQuery(id+"F0.wireOp",EDGE,"E4.3.1");Q12=makeQuery(id+"F0.imprint","IMPRINT",FACE,{"disambiguationData":[TD([[makeQuery(id+"F0.imprint","IMPRINT",EDGE,{"derivedFrom":subQ1}),1.0]])]});}
            var Q13;
            {var subQ1=sQuery(id+"F0.wireOp",EDGE,"E4.2.1");Q13=makeQuery(id+"F0.imprint","IMPRINT",FACE,{"disambiguationData":[TD([[makeQuery(id+"F0.imprint","IMPRINT",EDGE,{"derivedFrom":subQ1}),1.0]])]});}
            var Q14;
            {var subQ0=sQuery(id+"F0.wireOp",EDGE,"E4.2.4");Q14=makeQuery(id+"F0.imprint","IMPRINT",FACE,{"disambiguationData":[TD([[makeQuery(id+"F0.imprint","IMPRINT",EDGE,{"derivedFrom":subQ0}),-1.0]])]});}
            var Q15;
            {var subQ0=sQuery(id+"F0.wireOp",EDGE,"E4.1.4");Q15=makeQuery(id+"F0.imprint","IMPRINT",FACE,{"disambiguationData":[TD([[makeQuery(id+"F0.imprint","IMPRINT",EDGE,{"derivedFrom":subQ0}),-1.0]])]});}
            var Q16;
            {var subQ1=sQuery(id+"F0.wireOp",EDGE,"E4.1.1");Q16=makeQuery(id+"F0.imprint","IMPRINT",FACE,{"disambiguationData":[TD([[makeQuery(id+"F0.imprint","IMPRINT",EDGE,{"derivedFrom":subQ1}),1.0]])]});}
            var Q17;
            {var subQ1=sQuery(id+"F0.wireOp",EDGE,"E2.filletArc");Q17=makeQuery(id+"F0.imprint","IMPRINT",FACE,{"disambiguationData":[TD([[makeQuery(id+"F0.imprint","IMPRINT",EDGE,{"derivedFrom":subQ1}),1.0]])]});}
            var Q18;
            {var subQ0=sQuery(id+"F0.wireOp",EDGE,"E1.top");Q18=makeQuery(id+"F0.imprint","IMPRINT",FACE,{"disambiguationData":[TD([[makeQuery(id+"F0.imprint","IMPRINT",EDGE,{"derivedFrom":subQ0}),-1.0]])]});}
            var Q19;
            {var subQ0=sQuery(id+"F0.wireOp",EDGE,"E4.36.4");Q19=makeQuery(id+"F0.imprint","IMPRINT",FACE,{"disambiguationData":[TD([[makeQuery(id+"F0.imprint","IMPRINT",EDGE,{"derivedFrom":subQ0}),-1.0]])]});}
            var Q20;
            {var subQ5=sQuery(id+"F0.wireOp",EDGE,"E4.36.1");Q20=makeQuery(id+"F0.imprint","IMPRINT",FACE,{"disambiguationData":[TD([[makeQuery(id+"F0.imprint","IMPRINT",EDGE,{"derivedFrom":subQ5}),1.0]])]});}
            var Q21;
            {var subQ1=sQuery(id+"F0.wireOp",EDGE,"E4.35.1");Q21=makeQuery(id+"F0.imprint","IMPRINT",FACE,{"disambiguationData":[TD([[makeQuery(id+"F0.imprint","IMPRINT",EDGE,{"derivedFrom":subQ1}),1.0]])]});}
            var Q22;
            {var subQ0=sQuery(id+"F0.wireOp",EDGE,"E4.35.4");Q22=makeQuery(id+"F0.imprint","IMPRINT",FACE,{"disambiguationData":[TD([[makeQuery(id+"F0.imprint","IMPRINT",EDGE,{"derivedFrom":subQ0}),-1.0]])]});}
            var Q23;
            {var subQ0=sQuery(id+"F0.wireOp",EDGE,"E4.34.4");Q23=makeQuery(id+"F0.imprint","IMPRINT",FACE,{"disambiguationData":[TD([[makeQuery(id+"F0.imprint","IMPRINT",EDGE,{"derivedFrom":subQ0}),-1.0]])]});}
            var Q24;
            {var subQ1=sQuery(id+"F0.wireOp",EDGE,"E4.34.1");Q24=makeQuery(id+"F0.imprint","IMPRINT",FACE,{"disambiguationData":[TD([[makeQuery(id+"F0.imprint","IMPRINT",EDGE,{"derivedFrom":subQ1}),1.0]])]});}
            var Q25;
            {var subQ1=sQuery(id+"F0.wireOp",EDGE,"E4.33.1");Q25=makeQuery(id+"F0.imprint","IMPRINT",FACE,{"disambiguationData":[TD([[makeQuery(id+"F0.imprint","IMPRINT",EDGE,{"derivedFrom":subQ1}),1.0]])]});}
            var Q26;
            {var subQ0=sQuery(id+"F0.wireOp",EDGE,"E4.33.4");Q26=makeQuery(id+"F0.imprint","IMPRINT",FACE,{"disambiguationData":[TD([[makeQuery(id+"F0.imprint","IMPRINT",EDGE,{"derivedFrom":subQ0}),-1.0]])]});}
            var Q27;
            {var subQ0=sQuery(id+"F0.wireOp",EDGE,"E4.32.4");Q27=makeQuery(id+"F0.imprint","IMPRINT",FACE,{"disambiguationData":[TD([[makeQuery(id+"F0.imprint","IMPRINT",EDGE,{"derivedFrom":subQ0}),-1.0]])]});}
            var Q28;
            {var subQ1=sQuery(id+"F0.wireOp",EDGE,"E4.32.1");Q28=makeQuery(id+"F0.imprint","IMPRINT",FACE,{"disambiguationData":[TD([[makeQuery(id+"F0.imprint","IMPRINT",EDGE,{"derivedFrom":subQ1}),1.0]])]});}
            var Q29;
            {var subQ1=sQuery(id+"F0.wireOp",EDGE,"E4.31.1");Q29=makeQuery(id+"F0.imprint","IMPRINT",FACE,{"disambiguationData":[TD([[makeQuery(id+"F0.imprint","IMPRINT",EDGE,{"derivedFrom":subQ1}),1.0]])]});}
            var Q30;
            {var subQ0=sQuery(id+"F0.wireOp",EDGE,"E4.31.4");Q30=makeQuery(id+"F0.imprint","IMPRINT",FACE,{"disambiguationData":[TD([[makeQuery(id+"F0.imprint","IMPRINT",EDGE,{"derivedFrom":subQ0}),-1.0]])]});}
            var Q31;
            {var subQ0=sQuery(id+"F0.wireOp",EDGE,"E4.9.4");Q31=makeQuery(id+"F0.imprint","IMPRINT",FACE,{"disambiguationData":[TD([[makeQuery(id+"F0.imprint","IMPRINT",EDGE,{"derivedFrom":subQ0}),-1.0]])]});}
            var Q32;
            {var subQ1=sQuery(id+"F0.wireOp",EDGE,"E4.9.1");Q32=makeQuery(id+"F0.imprint","IMPRINT",FACE,{"disambiguationData":[TD([[makeQuery(id+"F0.imprint","IMPRINT",EDGE,{"derivedFrom":subQ1}),1.0]])]});}
            var Q33;
            {var subQ1=sQuery(id+"F0.wireOp",EDGE,"E4.10.1");Q33=makeQuery(id+"F0.imprint","IMPRINT",FACE,{"disambiguationData":[TD([[makeQuery(id+"F0.imprint","IMPRINT",EDGE,{"derivedFrom":subQ1}),1.0]])]});}
            var Q34;
            {var subQ0=sQuery(id+"F0.wireOp",EDGE,"E4.10.4");Q34=makeQuery(id+"F0.imprint","IMPRINT",FACE,{"disambiguationData":[TD([[makeQuery(id+"F0.imprint","IMPRINT",EDGE,{"derivedFrom":subQ0}),-1.0]])]});}
            var Q35;
            {var subQ0=sQuery(id+"F0.wireOp",EDGE,"E4.11.4");Q35=makeQuery(id+"F0.imprint","IMPRINT",FACE,{"disambiguationData":[TD([[makeQuery(id+"F0.imprint","IMPRINT",EDGE,{"derivedFrom":subQ0}),-1.0]])]});}
            var Q36;
            {var subQ1=sQuery(id+"F0.wireOp",EDGE,"E4.11.1");Q36=makeQuery(id+"F0.imprint","IMPRINT",FACE,{"disambiguationData":[TD([[makeQuery(id+"F0.imprint","IMPRINT",EDGE,{"derivedFrom":subQ1}),1.0]])]});}
            var Q37;
            {var subQ1=sQuery(id+"F0.wireOp",EDGE,"E4.12.1");Q37=makeQuery(id+"F0.imprint","IMPRINT",FACE,{"disambiguationData":[TD([[makeQuery(id+"F0.imprint","IMPRINT",EDGE,{"derivedFrom":subQ1}),1.0]])]});}
            var Q38;
            {var subQ0=sQuery(id+"F0.wireOp",EDGE,"E4.12.4");Q38=makeQuery(id+"F0.imprint","IMPRINT",FACE,{"disambiguationData":[TD([[makeQuery(id+"F0.imprint","IMPRINT",EDGE,{"derivedFrom":subQ0}),-1.0]])]});}
            var Q39;
            {var subQ0=sQuery(id+"F0.wireOp",EDGE,"E4.13.4");Q39=makeQuery(id+"F0.imprint","IMPRINT",FACE,{"disambiguationData":[TD([[makeQuery(id+"F0.imprint","IMPRINT",EDGE,{"derivedFrom":subQ0}),-1.0]])]});}
            var Q40;
            {var subQ1=sQuery(id+"F0.wireOp",EDGE,"E4.13.1");Q40=makeQuery(id+"F0.imprint","IMPRINT",FACE,{"disambiguationData":[TD([[makeQuery(id+"F0.imprint","IMPRINT",EDGE,{"derivedFrom":subQ1}),1.0]])]});}
            var Q41;
            {var subQ1=sQuery(id+"F0.wireOp",EDGE,"E4.14.1");Q41=makeQuery(id+"F0.imprint","IMPRINT",FACE,{"disambiguationData":[TD([[makeQuery(id+"F0.imprint","IMPRINT",EDGE,{"derivedFrom":subQ1}),1.0]])]});}
            var Q42;
            {var subQ0=sQuery(id+"F0.wireOp",EDGE,"E4.14.4");Q42=makeQuery(id+"F0.imprint","IMPRINT",FACE,{"disambiguationData":[TD([[makeQuery(id+"F0.imprint","IMPRINT",EDGE,{"derivedFrom":subQ0}),-1.0]])]});}
            var Q43;
            {var subQ0=sQuery(id+"F0.wireOp",EDGE,"E4.15.4");Q43=makeQuery(id+"F0.imprint","IMPRINT",FACE,{"disambiguationData":[TD([[makeQuery(id+"F0.imprint","IMPRINT",EDGE,{"derivedFrom":subQ0}),-1.0]])]});}
            var Q44;
            {var subQ1=sQuery(id+"F0.wireOp",EDGE,"E4.15.1");Q44=makeQuery(id+"F0.imprint","IMPRINT",FACE,{"disambiguationData":[TD([[makeQuery(id+"F0.imprint","IMPRINT",EDGE,{"derivedFrom":subQ1}),1.0]])]});}
            var Q45;
            {var subQ0=sQuery(id+"F0.wireOp",EDGE,"E4.16.4");Q45=makeQuery(id+"F0.imprint","IMPRINT",FACE,{"disambiguationData":[TD([[makeQuery(id+"F0.imprint","IMPRINT",EDGE,{"derivedFrom":subQ0}),-1.0]])]});}
            var Q46;
            {var subQ1=sQuery(id+"F0.wireOp",EDGE,"E4.16.1");Q46=makeQuery(id+"F0.imprint","IMPRINT",FACE,{"disambiguationData":[TD([[makeQuery(id+"F0.imprint","IMPRINT",EDGE,{"derivedFrom":subQ1}),1.0]])]});}
            var Q47;
            {var subQ1=sQuery(id+"F0.wireOp",EDGE,"E4.17.1");Q47=makeQuery(id+"F0.imprint","IMPRINT",FACE,{"disambiguationData":[TD([[makeQuery(id+"F0.imprint","IMPRINT",EDGE,{"derivedFrom":subQ1}),1.0]])]});}
            var Q48;
            {var subQ0=sQuery(id+"F0.wireOp",EDGE,"E4.17.4");Q48=makeQuery(id+"F0.imprint","IMPRINT",FACE,{"disambiguationData":[TD([[makeQuery(id+"F0.imprint","IMPRINT",EDGE,{"derivedFrom":subQ0}),-1.0]])]});}
            var Q49;
            {var subQ0=sQuery(id+"F0.wireOp",EDGE,"E4.18.4");Q49=makeQuery(id+"F0.imprint","IMPRINT",FACE,{"disambiguationData":[TD([[makeQuery(id+"F0.imprint","IMPRINT",EDGE,{"derivedFrom":subQ0}),-1.0]])]});}
            var Q50;
            {var subQ1=sQuery(id+"F0.wireOp",EDGE,"E4.18.1");Q50=makeQuery(id+"F0.imprint","IMPRINT",FACE,{"disambiguationData":[TD([[makeQuery(id+"F0.imprint","IMPRINT",EDGE,{"derivedFrom":subQ1}),1.0]])]});}
            var Q51;
            {var subQ1=sQuery(id+"F0.wireOp",EDGE,"E4.19.1");Q51=makeQuery(id+"F0.imprint","IMPRINT",FACE,{"disambiguationData":[TD([[makeQuery(id+"F0.imprint","IMPRINT",EDGE,{"derivedFrom":subQ1}),1.0]])]});}
            var Q52;
            {var subQ0=sQuery(id+"F0.wireOp",EDGE,"E4.19.4");Q52=makeQuery(id+"F0.imprint","IMPRINT",FACE,{"disambiguationData":[TD([[makeQuery(id+"F0.imprint","IMPRINT",EDGE,{"derivedFrom":subQ0}),-1.0]])]});}
            var Q53;
            {var subQ0=sQuery(id+"F0.wireOp",EDGE,"E4.20.4");Q53=makeQuery(id+"F0.imprint","IMPRINT",FACE,{"disambiguationData":[TD([[makeQuery(id+"F0.imprint","IMPRINT",EDGE,{"derivedFrom":subQ0}),-1.0]])]});}
            var Q54;
            {var subQ1=sQuery(id+"F0.wireOp",EDGE,"E4.20.1");Q54=makeQuery(id+"F0.imprint","IMPRINT",FACE,{"disambiguationData":[TD([[makeQuery(id+"F0.imprint","IMPRINT",EDGE,{"derivedFrom":subQ1}),1.0]])]});}
            var Q55;
            {var subQ6=sQuery(id+"F0.wireOp",EDGE,"E4.21.1");Q55=makeQuery(id+"F0.imprint","IMPRINT",FACE,{"disambiguationData":[TD([[makeQuery(id+"F0.imprint","IMPRINT",EDGE,{"derivedFrom":subQ6}),1.0]])]});}
            var Q56;
            {var subQ0=sQuery(id+"F0.wireOp",EDGE,"E4.21.4");Q56=makeQuery(id+"F0.imprint","IMPRINT",FACE,{"disambiguationData":[TD([[makeQuery(id+"F0.imprint","IMPRINT",EDGE,{"derivedFrom":subQ0}),-1.0]])]});}
            var Q57;
            {var subQ0=sQuery(id+"F0.wireOp",EDGE,"E4.22.4");Q57=makeQuery(id+"F0.imprint","IMPRINT",FACE,{"disambiguationData":[TD([[makeQuery(id+"F0.imprint","IMPRINT",EDGE,{"derivedFrom":subQ0}),-1.0]])]});}
            var Q58;
            {var subQ1=sQuery(id+"F0.wireOp",EDGE,"E4.22.1");Q58=makeQuery(id+"F0.imprint","IMPRINT",FACE,{"disambiguationData":[TD([[makeQuery(id+"F0.imprint","IMPRINT",EDGE,{"derivedFrom":subQ1}),1.0]])]});}
            var Q59;
            {var subQ1=sQuery(id+"F0.wireOp",EDGE,"E4.23.1");Q59=makeQuery(id+"F0.imprint","IMPRINT",FACE,{"disambiguationData":[TD([[makeQuery(id+"F0.imprint","IMPRINT",EDGE,{"derivedFrom":subQ1}),1.0]])]});}
            var Q60;
            {var subQ0=sQuery(id+"F0.wireOp",EDGE,"E4.23.4");Q60=makeQuery(id+"F0.imprint","IMPRINT",FACE,{"disambiguationData":[TD([[makeQuery(id+"F0.imprint","IMPRINT",EDGE,{"derivedFrom":subQ0}),-1.0]])]});}
            var Q61;
            {var subQ0=sQuery(id+"F0.wireOp",EDGE,"E4.24.4");Q61=makeQuery(id+"F0.imprint","IMPRINT",FACE,{"disambiguationData":[TD([[makeQuery(id+"F0.imprint","IMPRINT",EDGE,{"derivedFrom":subQ0}),-1.0]])]});}
            var Q62;
            {var subQ1=sQuery(id+"F0.wireOp",EDGE,"E4.24.1");Q62=makeQuery(id+"F0.imprint","IMPRINT",FACE,{"disambiguationData":[TD([[makeQuery(id+"F0.imprint","IMPRINT",EDGE,{"derivedFrom":subQ1}),1.0]])]});}
            var Q63;
            {var subQ1=sQuery(id+"F0.wireOp",EDGE,"E4.25.1");Q63=makeQuery(id+"F0.imprint","IMPRINT",FACE,{"disambiguationData":[TD([[makeQuery(id+"F0.imprint","IMPRINT",EDGE,{"derivedFrom":subQ1}),1.0]])]});}
            var Q64;
            {var subQ0=sQuery(id+"F0.wireOp",EDGE,"E4.25.4");Q64=makeQuery(id+"F0.imprint","IMPRINT",FACE,{"disambiguationData":[TD([[makeQuery(id+"F0.imprint","IMPRINT",EDGE,{"derivedFrom":subQ0}),-1.0]])]});}
            var Q65;
            {var subQ0=sQuery(id+"F0.wireOp",EDGE,"E4.26.4");Q65=makeQuery(id+"F0.imprint","IMPRINT",FACE,{"disambiguationData":[TD([[makeQuery(id+"F0.imprint","IMPRINT",EDGE,{"derivedFrom":subQ0}),-1.0]])]});}
            var Q66;
            {var subQ1=sQuery(id+"F0.wireOp",EDGE,"E4.26.1");Q66=makeQuery(id+"F0.imprint","IMPRINT",FACE,{"disambiguationData":[TD([[makeQuery(id+"F0.imprint","IMPRINT",EDGE,{"derivedFrom":subQ1}),1.0]])]});}
            var Q67;
            {var subQ1=sQuery(id+"F0.wireOp",EDGE,"E4.27.1");Q67=makeQuery(id+"F0.imprint","IMPRINT",FACE,{"disambiguationData":[TD([[makeQuery(id+"F0.imprint","IMPRINT",EDGE,{"derivedFrom":subQ1}),1.0]])]});}
            var Q68;
            {var subQ0=sQuery(id+"F0.wireOp",EDGE,"E4.27.4");Q68=makeQuery(id+"F0.imprint","IMPRINT",FACE,{"disambiguationData":[TD([[makeQuery(id+"F0.imprint","IMPRINT",EDGE,{"derivedFrom":subQ0}),-1.0]])]});}
            var Q69;
            {var subQ0=sQuery(id+"F0.wireOp",EDGE,"E4.28.4");Q69=makeQuery(id+"F0.imprint","IMPRINT",FACE,{"disambiguationData":[TD([[makeQuery(id+"F0.imprint","IMPRINT",EDGE,{"derivedFrom":subQ0}),-1.0]])]});}
            var Q70;
            {var subQ4=sQuery(id+"F0.wireOp",EDGE,"E4.28.1");Q70=makeQuery(id+"F0.imprint","IMPRINT",FACE,{"disambiguationData":[TD([[makeQuery(id+"F0.imprint","IMPRINT",EDGE,{"derivedFrom":subQ4}),1.0]])]});}
            var Q71;
            {var subQ0=sQuery(id+"F0.wireOp",EDGE,"E4.29.4");Q71=makeQuery(id+"F0.imprint","IMPRINT",FACE,{"disambiguationData":[TD([[makeQuery(id+"F0.imprint","IMPRINT",EDGE,{"derivedFrom":subQ0}),-1.0]])]});}
            var Q72;
            {var subQ1=sQuery(id+"F0.wireOp",EDGE,"E4.29.1");Q72=makeQuery(id+"F0.imprint","IMPRINT",FACE,{"disambiguationData":[TD([[makeQuery(id+"F0.imprint","IMPRINT",EDGE,{"derivedFrom":subQ1}),1.0]])]});}
            var Q73;
            {var subQ0=sQuery(id+"F0.wireOp",EDGE,"E4.30.4");Q73=makeQuery(id+"F0.imprint","IMPRINT",FACE,{"disambiguationData":[TD([[makeQuery(id+"F0.imprint","IMPRINT",EDGE,{"derivedFrom":subQ0}),-1.0]])]});}
            var Q74;
            {var subQ1=sQuery(id+"F0.wireOp",EDGE,"E4.30.1");Q74=makeQuery(id+"F0.imprint","IMPRINT",FACE,{"disambiguationData":[TD([[makeQuery(id+"F0.imprint","IMPRINT",EDGE,{"derivedFrom":subQ1}),1.0]])]});}
            extrude(context, id + "F1", {"entities" : qUnion([Q0, Q1, Q2, Q3, Q4, Q5, Q6, Q7, Q8, Q9, Q10, Q11, Q12, Q13, Q14, Q15, Q16, Q17, Q18, Q19, Q20, Q21, Q22, Q23, Q24, Q25, Q26, Q27, Q28, Q29, Q30, Q31, Q32, Q33, Q34, Q35, Q36, Q37, Q38, Q39, Q40, Q41, Q42, Q43, Q44, Q45, Q46, Q47, Q48, Q49, Q50, Q51, Q52, Q53, Q54, Q55, Q56, Q57, Q58, Q59, Q60, Q61, Q62, Q63, Q64, Q65, Q66, Q67, Q68, Q69, Q70, Q71, Q72, Q73, Q74]), "depth" : 5 * mm});
        }
    });
